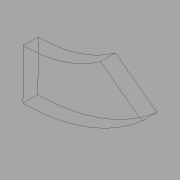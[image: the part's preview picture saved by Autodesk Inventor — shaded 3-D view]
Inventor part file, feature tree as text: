
AUTODESK INVENTOR PART (.ipt)
format: ipt  version: 2022.1 (Build 261234020, 234B)  size: 93,696 bytes
history: imported  units: in
note: dims shown in document units (in); Inventor stores cm internally (conversion verified against a paired STEP export)
features: imported_body x1
ambient origin geometry x8: Origin, YZ Plane, XZ Plane, XY Plane, X Axis, Y Axis, Z Axis, Center Point
bodies: Solid1 (imported_parasolid), Body1 (imported_parasolid)
feature tree (1):
  imported_body  NMx_Import_Brep_tag  [imported B-rep: ~6 faces, bbox_mm=[1213.186396, 761.386567, 152.4]]
